# Revit family: QF-Buffer_Tank-OptiPure-16G BUFF_HF PLUS_1IN OUT
name_source: partatom
category: Specialty Equipment
revit_build: Autodesk Revit 2017 (Build: 20160225_1515(x64)
units: mm (PartAtom-declared; Revit-internal decimal feet)

## family parameters
Always vertical = Yes
Cut with Voids When Loaded = No
OmniClass Number = 23.40.40.14
OmniClass Title = Food Service Equipment
Part Type = Normal
Room Calculation Point = No
Round Connector Dimension = Use Diameter
Shared = No
Work Plane-Based = No

## types (1)
- 16G BUFF-HF PLUS-1IN OUT
    Assembly Code = E1090300
    Description = BUFFER TANK
    Filtered Water In = 0.5 "
    Filtered Water Supply Size = 1"
    Height = 30.35 "
    Keynote = 11400
    Length = 15.62 "
    Manufacturer = OPTIPURE
    Material = Blue Plastic
    Model = 16G BUFF-HF PLUS-1IN OUT
    URL = WWW.OPTIPUREWATER.COM
    Valve Material = Plastic
    Width = 15.62 "

## geometry (parser evidence)
native form markers: Sweep x3
no freeform markers — native parametric forms only
